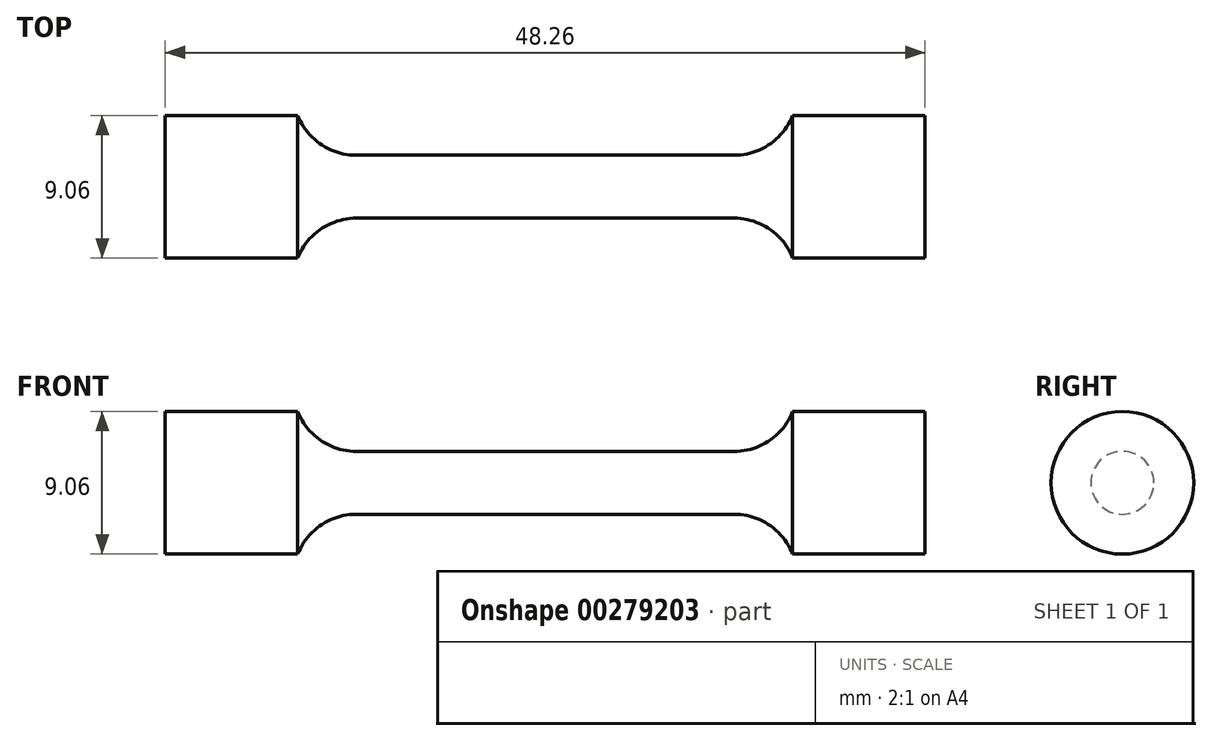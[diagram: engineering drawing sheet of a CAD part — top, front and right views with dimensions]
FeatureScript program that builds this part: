
annotation { "Feature Type Name" : "Feature", "Feature Type Description" : "" }
export const myFeature = defineFeature(function(context is Context, id is Id, definition is map)
    precondition{}
    {
        {
            var Q0;
            Q0=qCreatedBy(makeId("Front.planeOp"),FACE);
            var sketch = newSketch(context, id + "F0", { "sketchPlane" : qUnion([Q0])});
            skLineSegment(sketch, "E0", {"start": v(0, 2) * mm, "end": v(12, 2) * mm});
            skArc(sketch, "E1", {"start": v(12, 2) * mm, "mid": v(14.25, 2.7) * mm, "end": v(15.72, 4.53) * mm});
            skLineSegment(sketch, "E2", {"start": v(15.72, 4.53) * mm, "end": v(24.13, 4.53) * mm});
            skLineSegment(sketch, "E3", {"start": v(24.13, 0) * mm, "end": v(24.13, 4.53) * mm});
            skLineSegment(sketch, "E4.MirrorCS", {"start": v(0, 2) * mm, "end": v(-12, 2) * mm});
            skLineSegment(sketch, "E5.MirrorCS", {"start": v(-24.13, 0) * mm, "end": v(-24.13, 4.53) * mm});
            skLineSegment(sketch, "E6.MirrorCS", {"start": v(-15.72, 4.53) * mm, "end": v(-24.13, 4.53) * mm});
            skArc(sketch, "E7.MirrorCS", {"start": v(-12, 2) * mm, "mid": v(-14.25, 2.7) * mm, "end": v(-15.72, 4.53) * mm});
            skLineSegment(sketch, "E8", {"start": v(-24.13, 0) * mm, "end": v(24.13, 0) * mm});
            skSolve(sketch);
        }
        {
            var Q0;
            Q0=makeQuery(id+"F0.imprint","IMPRINT",FACE,{"disambiguationData":[TD([[makeQuery(id+"F0.imprint","IMPRINT",EDGE,{"derivedFrom":sQuery(id+"F0.wireOp",EDGE,"E0")}),-1.0]])]});
            var Q1;
            Q1=sQuery(id+"F0.wireOp",EDGE,"E8");
            revolve(context, id + "F1", {"entities" : qUnion([Q0]), "axis" : qUnion([Q1]), "revolveType" : RevolveType.FULL});
        }
    });
